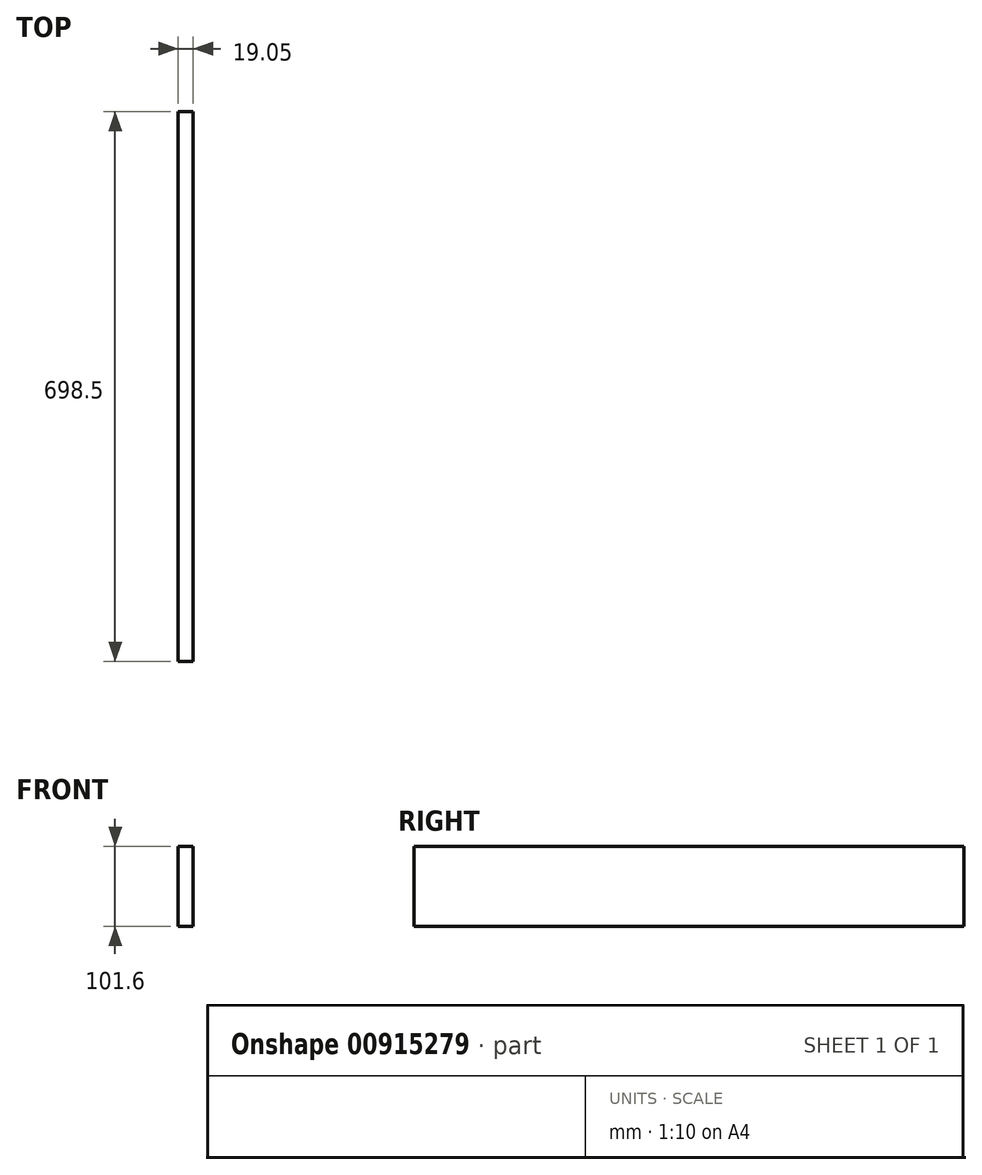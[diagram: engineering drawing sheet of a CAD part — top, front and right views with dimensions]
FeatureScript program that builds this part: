
annotation { "Feature Type Name" : "Feature", "Feature Type Description" : "" }
export const myFeature = defineFeature(function(context is Context, id is Id, definition is map)
    precondition{}
    {
        {
            var Q0;
            Q0=qCreatedBy(makeId("Right.planeOp"),FACE);
            var sketch = newSketch(context, id + "F0", { "sketchPlane" : qUnion([Q0])});
            skLineSegment(sketch, "E0.bottom", {"start": v(-349.25, 50.8) * mm, "end": v(349.25, 50.8) * mm});
            skLineSegment(sketch, "E0.top", {"start": v(-349.25, -50.8) * mm, "end": v(349.25, -50.8) * mm});
            skLineSegment(sketch, "E0.left", {"start": v(-349.25, 50.8) * mm, "end": v(-349.25, -50.8) * mm});
            skLineSegment(sketch, "E0.right", {"start": v(349.25, 50.8) * mm, "end": v(349.25, -50.8) * mm});
            skPoint(sketch, "E0.middle", {"position": v(0, 0) * mm});
            skSolve(sketch);
        }
        {
            var Q0;
            Q0=makeQuery(id+"F0.imprint","IMPRINT",FACE,{"disambiguationData":[TD([[makeQuery(id+"F0.imprint","IMPRINT",EDGE,{"derivedFrom":sQuery(id+"F0.wireOp",EDGE,"E0.bottom")}),-1.0]])]});
            extrude(context, id + "F1", {"entities" : qUnion([Q0]), "depth" : 19.05 * mm, "offsetDistance" : 25.4 * mm});
        }
    });
